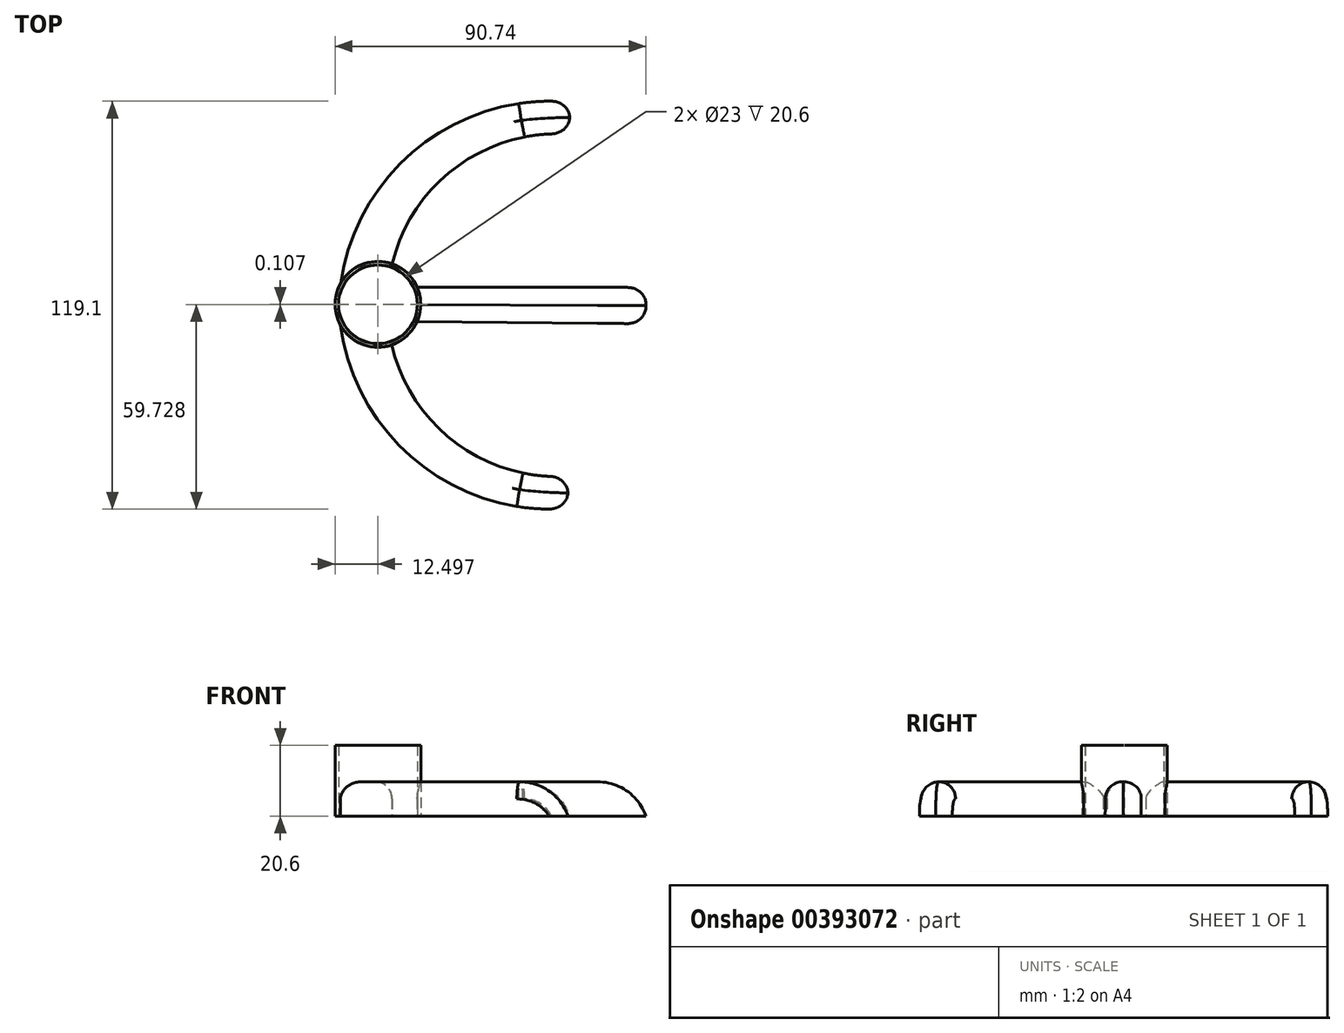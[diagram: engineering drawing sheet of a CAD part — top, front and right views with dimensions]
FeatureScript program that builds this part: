
annotation { "Feature Type Name" : "Feature", "Feature Type Description" : "" }
export const myFeature = defineFeature(function(context is Context, id is Id, definition is map)
    precondition{}
    {
        {
            var Q0;
            Q0=qCreatedBy(makeId("Top.planeOp"),FACE);
            var sketch = newSketch(context, id + "F0", { "sketchPlane" : qUnion([Q0])});
            skCircle(sketch, "E0", {"center": v(-38.8, -35.9) * mm, "radius": 12.5 * mm});
            skCircle(sketch, "E1", {"center": v(-38.8, -35.9) * mm, "radius": 11.5 * mm});
            skArc(sketch, "E2", {"start": v(17.18, 13.7) * mm, "mid": v(-15.68, 4.31) * mm, "end": v(-34.64, -24.1) * mm});
            skLineSegment(sketch, "E3", {"start": v(17.18, 13.7) * mm, "end": v(17.18, 23.12) * mm});
            skArc(sketch, "E4", {"start": v(17.18, 23.12) * mm, "mid": v(-26.76, 10.04) * mm, "end": v(-49.65, -29.68) * mm});
            skLineSegment(sketch, "E5", {"start": v(39.44, -41.62) * mm, "end": v(39.44, -31) * mm});
            skLineSegment(sketch, "E6", {"start": v(39.44, -31) * mm, "end": v(-27.3, -31) * mm});
            skLineSegment(sketch, "E7", {"start": v(39.44, -36.31) * mm, "end": v(-50.3, -35.9) * mm});
            skLineSegment(sketch, "E8", {"start": v(-26.3, -36) * mm, "end": v(-27.3, -36) * mm});
            skSolve(sketch);
        }
        {
            var Q0;
            {var subQ0=sQuery(id+"F0.wireOp",EDGE,"E2");Q0=makeQuery(id+"F0.imprint","IMPRINT",FACE,{"disambiguationData":[TD([[makeQuery(id+"F0.imprint","IMPRINT",EDGE,{"derivedFrom":subQ0}),-1.0]])]});}
            extrude(context, id + "F1", {"entities" : qUnion([Q0]), "depth" : 10 * mm});
        }
        {
            var Q0;
            Q0=makeQuery(id+"F1.opExtrude","CAP_EDGE",EDGE,{"disambiguationData":[OSD([sQuery(id+"F0.wireOp",EDGE,"E3")])],"isStart":false});
            fillet(context, id + "F2", {"entities" : qUnion([Q0]), "radius" : 15 * mm, "tangentPropagation" : true, "allowEdgeOverflow" : false});
        }
        {
            var Q0;
            Q0=makeQuery(id+"F1.opExtrude","CAP_EDGE",EDGE,{"disambiguationData":[OSD([sQuery(id+"F0.wireOp",EDGE,"E2")])],"isStart":false});
            var Q1;
            Q1=makeQuery(id+"F1.opExtrude","CAP_EDGE",EDGE,{"disambiguationData":[OSD([sQuery(id+"F0.wireOp",EDGE,"E4")])],"isStart":false});
            fillet(context, id + "F3", {"entities" : qUnion([Q0, Q1]), "radius" : 5 * mm, "tangentPropagation" : true, "allowEdgeOverflow" : false});
        }
        {
            var Q0;
            Q0=makeQuery(id+"F0.imprint","IMPRINT",FACE,{"disambiguationData":[TD([[makeQuery(id+"F0.imprint","IMPRINT",EDGE,{"derivedFrom":sQuery(id+"F0.wireOp",EDGE,"E1")}),-1.0]])]});
            extrude(context, id + "F4", {"entities" : qUnion([Q0]), "operationType" : NewBodyOperationType.ADD, "depth" : 20.6 * mm});
        }
        {
            var Q0;
            {var subQ0=sQuery(id+"F0.wireOp",EDGE,"E6");Q0=makeQuery(id+"F0.imprint","IMPRINT",FACE,{"disambiguationData":[TD([[makeQuery(id+"F0.imprint","IMPRINT",EDGE,{"derivedFrom":subQ0}),1.0]])]});}
            extrude(context, id + "F5", {"entities" : qUnion([Q0]), "operationType" : NewBodyOperationType.ADD, "depth" : 10 * mm});
        }
        {
            var Q0;
            Q0=makeQuery(id+"F1.opExtrude","SWEPT_BODY",BODY,{"disambiguationData":[OSD([sQuery(id+"F0.wireOp",EDGE,"E0"),sQuery(id+"F0.wireOp",EDGE,"E2"),sQuery(id+"F0.wireOp",EDGE,"E3"),sQuery(id+"F0.wireOp",EDGE,"E4")])]});
            var Q1;
            Q1=makeQuery(id+"F5.opExtrude","SWEPT_FACE",FACE,{"disambiguationData":[OSD([sQuery(id+"F0.wireOp",EDGE,"E7")])]});
            mirror(context, id + "F6", {"entities" : qUnion([Q0]), "mirrorPlane" : qUnion([Q1])});
        }
        {
            var Q0;
            Q0=makeQuery(id+"F5.opExtrude","CAP_EDGE",EDGE,{"disambiguationData":[OSD([sQuery(id+"F0.wireOp",EDGE,"E5")])],"isStart":false});
            var Q1;
            Q1=makeQuery(id+"F6.opPattern","COPY",EDGE,{"derivedFrom":makeQuery(id+"F5.opExtrude","CAP_EDGE",EDGE,{"disambiguationData":[OSD([sQuery(id+"F0.wireOp",EDGE,"E5")])],"isStart":false}),"instanceName":"1"});
            fillet(context, id + "F7", {"entities" : qUnion([Q0, Q1]), "radius" : 15 * mm, "tangentPropagation" : true, "allowEdgeOverflow" : false});
        }
        {
            var Q0;
            Q0=makeQuery(id+"F5.opExtrude","CAP_EDGE",EDGE,{"disambiguationData":[OSD([sQuery(id+"F0.wireOp",EDGE,"E6")])],"isStart":false});
            var Q1;
            Q1=makeQuery(id+"F6.opPattern","COPY",EDGE,{"derivedFrom":makeQuery(id+"F5.opExtrude","CAP_EDGE",EDGE,{"disambiguationData":[OSD([sQuery(id+"F0.wireOp",EDGE,"E6")])],"isStart":false}),"instanceName":"1"});
            fillet(context, id + "F8", {"entities" : qUnion([Q0, Q1]), "radius" : 5 * mm, "tangentPropagation" : true, "allowEdgeOverflow" : false});
        }
        {
            var Q0;
            {var subQ0=sQuery(id+"F0.wireOp",EDGE,"E7");var subQ1=sQuery(id+"F0.wireOp",EDGE,"E1");var subQ2=makeQuery(id+"F0.imprint","INTERSECT",VERTEX,{"disambiguationData":[OD(0.0)],"derivedFrom":[subQ1,subQ0]});Q0=makeQuery(id+"F0.imprint","IMPRINT",FACE,{"disambiguationData":[TD([[makeQuery(id+"F0.imprint","IMPRINT",EDGE,{"disambiguationData":[TD([[subQ2,-1.0]])],"derivedFrom":subQ1}),1.0]])]});}
            var Q1;
            {var subQ0=sQuery(id+"F0.wireOp",EDGE,"E7");var subQ1=sQuery(id+"F0.wireOp",EDGE,"E1");var subQ2=makeQuery(id+"F0.imprint","INTERSECT",VERTEX,{"disambiguationData":[OD(0.0)],"derivedFrom":[subQ1,subQ0]});Q1=makeQuery(id+"F0.imprint","IMPRINT",FACE,{"disambiguationData":[TD([[makeQuery(id+"F0.imprint","IMPRINT",EDGE,{"disambiguationData":[TD([[subQ2,1.0]])],"derivedFrom":subQ1}),1.0]])]});}
            extrude(context, id + "F9", {"entities" : qUnion([Q0, Q1]), "depth" : 0.1 * mm});
        }
    });
